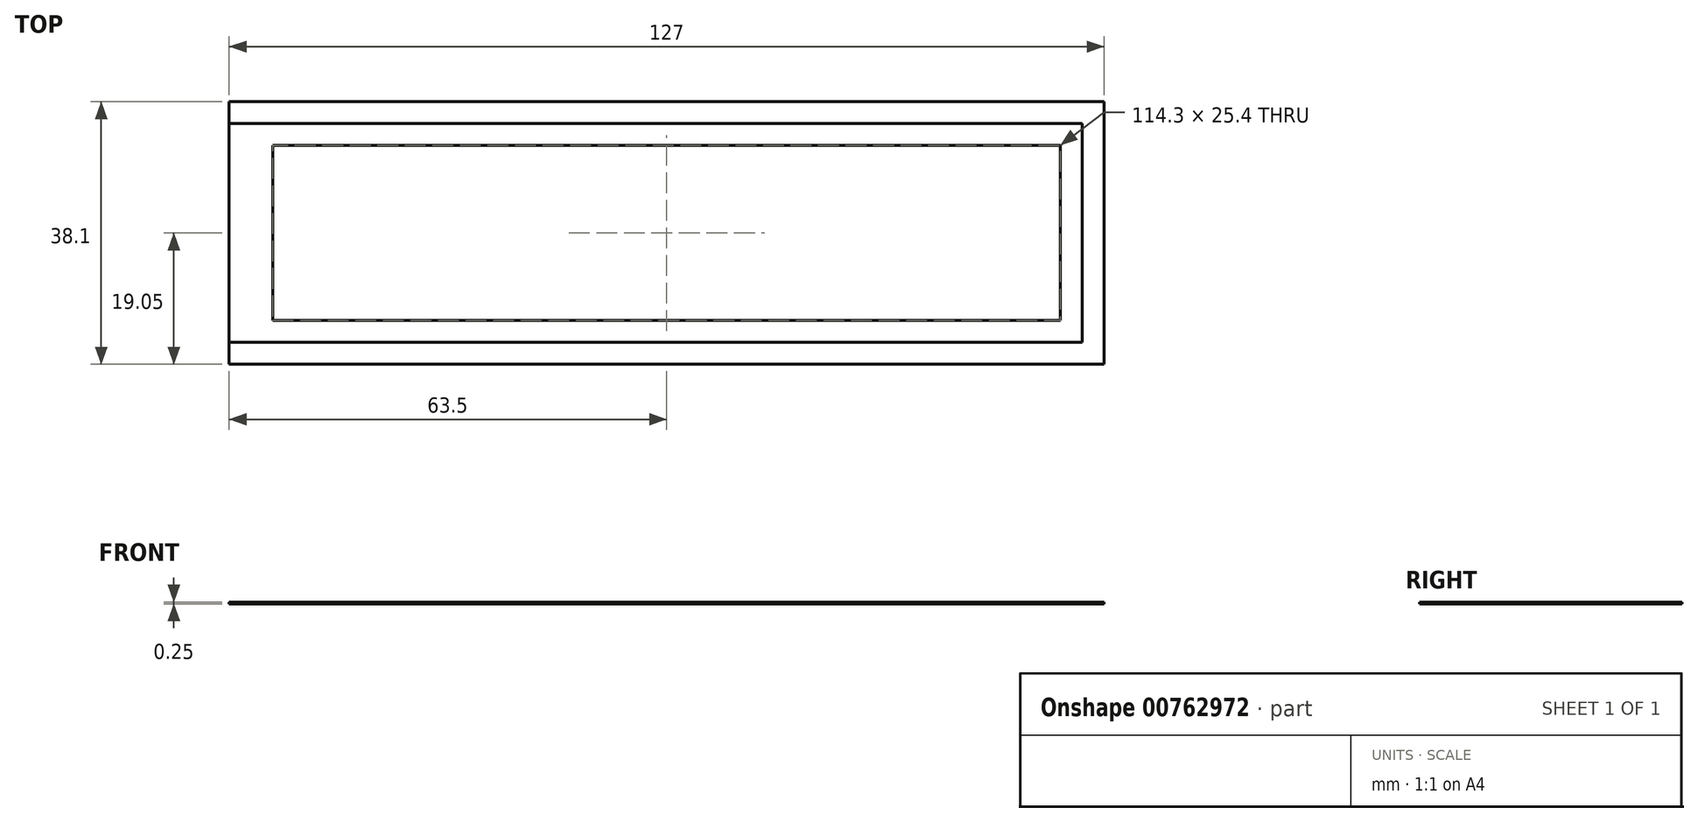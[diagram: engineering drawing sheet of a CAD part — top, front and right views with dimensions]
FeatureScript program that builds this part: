
annotation { "Feature Type Name" : "Feature", "Feature Type Description" : "" }
export const myFeature = defineFeature(function(context is Context, id is Id, definition is map)
    precondition{}
    {
        {
            assignVariable(context, id + "F0", {"name" : "t", "anyValue" : 0.25});
        }
        {
            var Q0;
            Q0=qCreatedBy(makeId("Top.planeOp"),FACE);
            var sketch = newSketch(context, id + "F1", { "sketchPlane" : qUnion([Q0])});
            skLineSegment(sketch, "E0.bottom", {"start": v(63.5, -19.05) * mm, "end": v(-63.5, -19.05) * mm});
            skLineSegment(sketch, "E0.top", {"start": v(63.5, 19.05) * mm, "end": v(-63.5, 19.05) * mm});
            skLineSegment(sketch, "E0.left", {"start": v(63.5, -19.05) * mm, "end": v(63.5, 19.05) * mm});
            skLineSegment(sketch, "E0.right", {"start": v(-63.5, -19.05) * mm, "end": v(-63.5, 19.05) * mm});
            skPoint(sketch, "E0.middle", {"position": v(0, 0) * mm});
            skLineSegment(sketch, "E1.bottom", {"start": v(57.15, -12.7) * mm, "end": v(-57.15, -12.7) * mm});
            skLineSegment(sketch, "E1.top", {"start": v(57.15, 12.7) * mm, "end": v(-57.15, 12.7) * mm});
            skLineSegment(sketch, "E1.left", {"start": v(57.15, -12.7) * mm, "end": v(57.15, 12.7) * mm});
            skLineSegment(sketch, "E1.right", {"start": v(-57.15, -12.7) * mm, "end": v(-57.15, 12.7) * mm});
            skLineSegment(sketch, "E2.bottom", {"start": v(-63.5, 15.88) * mm, "end": v(60.33, 15.88) * mm});
            skLineSegment(sketch, "E2.top", {"start": v(-63.5, -15.88) * mm, "end": v(60.33, -15.88) * mm});
            skLineSegment(sketch, "E2.left", {"start": v(-63.5, 15.88) * mm, "end": v(-63.5, -15.88) * mm});
            skLineSegment(sketch, "E2.right", {"start": v(60.33, 15.88) * mm, "end": v(60.33, -15.88) * mm});
            skPoint(sketch, "E2.middle", {"position": v(-1.59, 0) * mm});
            skSolve(sketch);
        }
        {
            var Q0;
            {var subQ3=sQuery(id+"F1.wireOp",EDGE,"E0.bottom");Q0=makeQuery(id+"F1.imprint","IMPRINT",FACE,{"disambiguationData":[TD([[makeQuery(id+"F1.imprint","IMPRINT",EDGE,{"derivedFrom":subQ3}),-1.0]])]});}
            var Q1;
            Q1=makeQuery(id+"F1.imprint","IMPRINT",FACE,{"disambiguationData":[TD([[makeQuery(id+"F1.imprint","IMPRINT",EDGE,{"derivedFrom":sQuery(id+"F1.wireOp",EDGE,"E1.bottom")}),-1.0]])]});
            var Q2;
            Q2=makeQuery(id+"F1.imprint","IMPRINT",FACE,{"disambiguationData":[TD([[makeQuery(id+"F1.imprint","IMPRINT",EDGE,{"derivedFrom":sQuery(id+"F1.wireOp",EDGE,"E1.bottom")}),1.0]])]});
            extrude(context, id + "F2", {"entities" : qUnion([Q0, Q1, Q2]), "depth" : (getVariable(context, 't')) * mm, "offsetDistance" : 25.4 * mm});
        }
        {
            var Q0;
            Q0=makeQuery(id+"F1.imprint","IMPRINT",FACE,{"disambiguationData":[TD([[makeQuery(id+"F1.imprint","IMPRINT",EDGE,{"derivedFrom":sQuery(id+"F1.wireOp",EDGE,"E1.bottom")}),1.0]])]});
            var Q1;
            {var subQ3=sQuery(id+"F1.wireOp",EDGE,"E0.bottom");Q1=makeQuery(id+"F1.imprint","IMPRINT",FACE,{"disambiguationData":[TD([[makeQuery(id+"F1.imprint","IMPRINT",EDGE,{"derivedFrom":subQ3}),-1.0]])]});}
            extrude(context, id + "F3", {"entities" : qUnion([Q0, Q1]), "depth" : (getVariable(context, 't')) * mm, "offsetDistance" : 25.4 * mm});
        }
        {
            var Q0;
            {var subQ3=sQuery(id+"F1.wireOp",EDGE,"E0.bottom");Q0=makeQuery(id+"F1.imprint","IMPRINT",FACE,{"disambiguationData":[TD([[makeQuery(id+"F1.imprint","IMPRINT",EDGE,{"derivedFrom":subQ3}),-1.0]])]});}
            extrude(context, id + "F4", {"entities" : qUnion([Q0]), "depth" : (getVariable(context, 't')) * mm, "offsetDistance" : 25.4 * mm});
        }
        {
            var Q0;
            Q0=makeQuery(id+"F1.imprint","IMPRINT",FACE,{"disambiguationData":[TD([[makeQuery(id+"F1.imprint","IMPRINT",EDGE,{"derivedFrom":sQuery(id+"F1.wireOp",EDGE,"E1.bottom")}),1.0]])]});
            var Q1;
            Q1=makeQuery(id+"F1.imprint","IMPRINT",FACE,{"disambiguationData":[TD([[makeQuery(id+"F1.imprint","IMPRINT",EDGE,{"derivedFrom":sQuery(id+"F1.wireOp",EDGE,"E1.bottom")}),-1.0]])]});
            extrude(context, id + "F5", {"entities" : qUnion([Q0, Q1]), "depth" : (getVariable(context, 't')) * mm, "offsetDistance" : 25.4 * mm});
        }
        {
            var Q0;
            Q0=makeQuery(id+"F1.imprint","IMPRINT",FACE,{"disambiguationData":[TD([[makeQuery(id+"F1.imprint","IMPRINT",EDGE,{"derivedFrom":sQuery(id+"F1.wireOp",EDGE,"E1.bottom")}),1.0]])]});
            var Q1;
            Q1=makeQuery(id+"F1.imprint","IMPRINT",FACE,{"disambiguationData":[TD([[makeQuery(id+"F1.imprint","IMPRINT",EDGE,{"derivedFrom":sQuery(id+"F1.wireOp",EDGE,"E1.bottom")}),-1.0]])]});
            var Q2;
            {var subQ3=sQuery(id+"F1.wireOp",EDGE,"E0.bottom");Q2=makeQuery(id+"F1.imprint","IMPRINT",FACE,{"disambiguationData":[TD([[makeQuery(id+"F1.imprint","IMPRINT",EDGE,{"derivedFrom":subQ3}),-1.0]])]});}
            extrude(context, id + "F6", {"entities" : qUnion([Q0, Q1, Q2]), "depth" : (getVariable(context, 't')) * mm, "offsetDistance" : 25.4 * mm});
        }
    });
